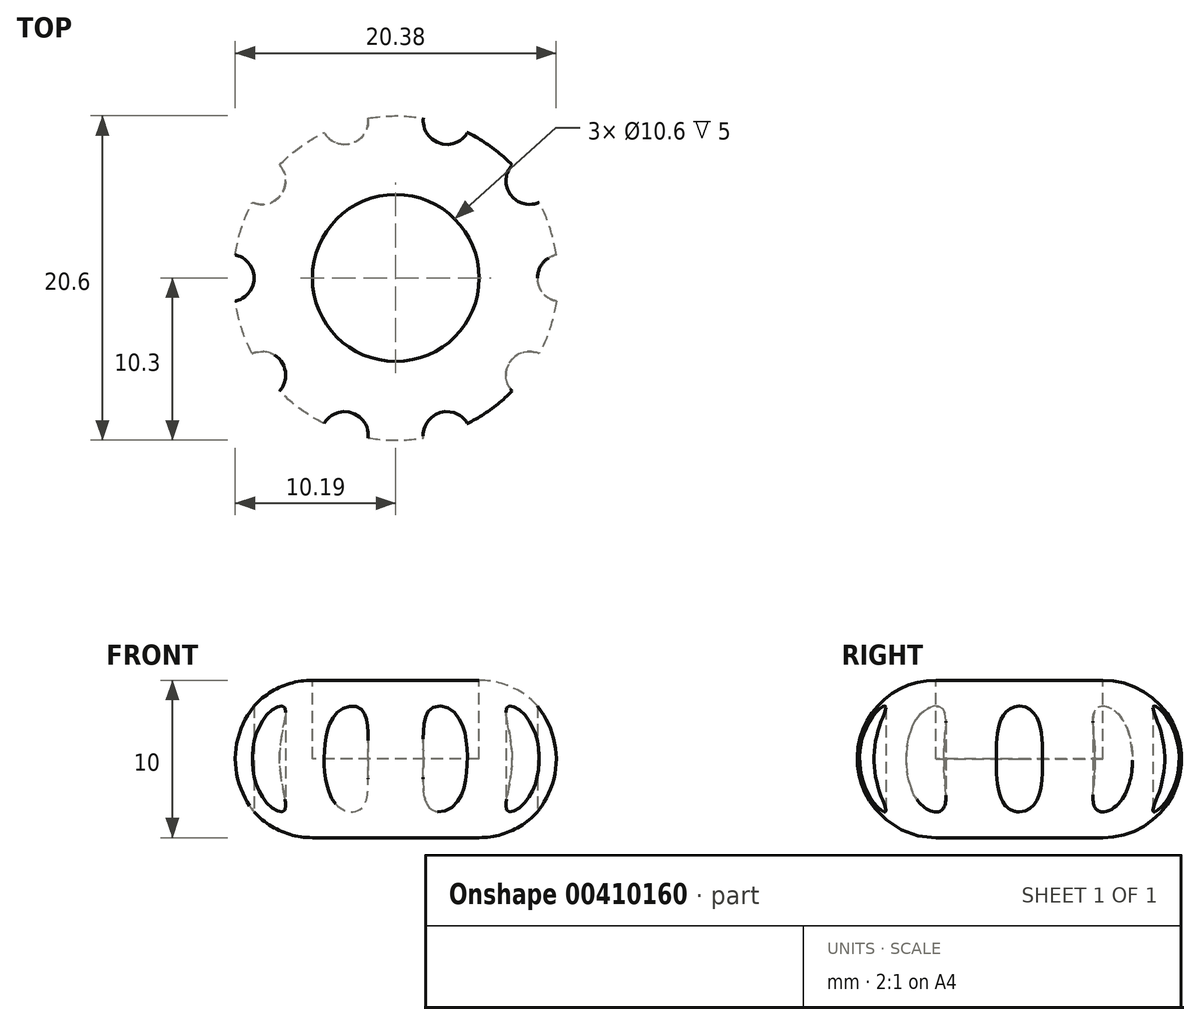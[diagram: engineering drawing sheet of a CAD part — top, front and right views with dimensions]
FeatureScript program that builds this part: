
annotation { "Feature Type Name" : "Feature", "Feature Type Description" : "" }
export const myFeature = defineFeature(function(context is Context, id is Id, definition is map)
    precondition{}
    {
        {
            var Q0;
            Q0=qCreatedBy(makeId("Front.planeOp"),FACE);
            var sketch = newSketch(context, id + "F0", { "sketchPlane" : qUnion([Q0])});
            skLineSegment(sketch, "E0", {"start": v(0, 0) * mm, "end": v(-5.3, 0) * mm});
            skLineSegment(sketch, "E1", {"start": v(-10.3, 5) * mm, "end": v(-10.3, 5) * mm});
            skLineSegment(sketch, "E2", {"start": v(-5.3, 10) * mm, "end": v(-5.3, 10) * mm});
            skLineSegment(sketch, "E3", {"start": v(-5.3, 10) * mm, "end": v(-5.3, 5) * mm});
            skLineSegment(sketch, "E4", {"start": v(-5.3, 5) * mm, "end": v(0, 5) * mm});
            skLineSegment(sketch, "E5", {"start": v(0, 5) * mm, "end": v(0, 0) * mm});
            skPoint(sketch, "E6.visualSharp", {"position": v(-10.3, 10) * mm});
            skArc(sketch, "E6.filletArc", {"start": v(-5.3, 10) * mm, "mid": v(-8.84, 8.54) * mm, "end": v(-10.3, 5) * mm});
            skPoint(sketch, "E7.visualSharp", {"position": v(-10.3, 0) * mm});
            skArc(sketch, "E7.filletArc", {"start": v(-10.3, 5) * mm, "mid": v(-8.84, 1.46) * mm, "end": v(-5.3, 0) * mm});
            skSolve(sketch);
        }
        {
            var Q0;
            Q0=makeQuery(id+"F0.imprint","IMPRINT",FACE,{"disambiguationData":[TD([[makeQuery(id+"F0.imprint","IMPRINT",EDGE,{"derivedFrom":sQuery(id+"F0.wireOp",EDGE,"E0")}),-1.0]])]});
            var Q1;
            Q1=sQuery(id+"F0.wireOp",EDGE,"E5");
            revolve(context, id + "F1", {"entities" : qUnion([Q0]), "axis" : qUnion([Q1]), "revolveType" : RevolveType.FULL});
        }
        {
            var Q0;
            Q0=makeQuery(id+"F1.opRevolve","SWEPT_FACE",FACE,{"disambiguationData":[OSD([sQuery(id+"F0.wireOp",EDGE,"E0")])]});
            var sketch = newSketch(context, id + "F2", { "sketchPlane" : qUnion([Q0])});
            skLineSegment(sketch, "E8", {"start": v(0, 0) * mm, "end": v(-16.48, 0) * mm, "construction": true});
            skCircle(sketch, "E9", {"center": v(-10.5, 0) * mm, "radius": 1.5 * mm});
            skCircle(sketch, "E10.1.0", {"center": v(-8.5, -6.17) * mm, "radius": 1.5 * mm});
            skCircle(sketch, "E10.2.0", {"center": v(-3.24, -9.99) * mm, "radius": 1.5 * mm});
            skCircle(sketch, "E10.3.0", {"center": v(3.24, -9.99) * mm, "radius": 1.5 * mm});
            skCircle(sketch, "E10.4.0", {"center": v(8.5, -6.17) * mm, "radius": 1.5 * mm});
            skCircle(sketch, "E10.5.0", {"center": v(10.5, 0) * mm, "radius": 1.5 * mm});
            skCircle(sketch, "E10.6.0", {"center": v(8.5, 6.17) * mm, "radius": 1.5 * mm});
            skCircle(sketch, "E10.7.0", {"center": v(3.24, 9.99) * mm, "radius": 1.5 * mm});
            skCircle(sketch, "E10.8.0", {"center": v(-3.24, 9.99) * mm, "radius": 1.5 * mm});
            skCircle(sketch, "E10.9.0", {"center": v(-8.5, 6.17) * mm, "radius": 1.5 * mm});
            skPoint(sketch, "E10.center", {"position": v(0, 0) * mm});
            skSolve(sketch);
        }
        {
            var Q0;
            Q0=makeQuery(id+"F2.imprint","IMPRINT",FACE,{"disambiguationData":[TD([[makeQuery(id+"F2.imprint","IMPRINT",EDGE,{"derivedFrom":sQuery(id+"F2.wireOp",EDGE,"E10.6.0")}),1.0]])]});
            var Q1;
            Q1=makeQuery(id+"F2.imprint","IMPRINT",FACE,{"disambiguationData":[TD([[makeQuery(id+"F2.imprint","IMPRINT",EDGE,{"derivedFrom":sQuery(id+"F2.wireOp",EDGE,"E10.5.0")}),1.0]])]});
            var Q2;
            Q2=makeQuery(id+"F2.imprint","IMPRINT",FACE,{"disambiguationData":[TD([[makeQuery(id+"F2.imprint","IMPRINT",EDGE,{"derivedFrom":sQuery(id+"F2.wireOp",EDGE,"E10.4.0")}),1.0]])]});
            var Q3;
            Q3=makeQuery(id+"F2.imprint","IMPRINT",FACE,{"disambiguationData":[TD([[makeQuery(id+"F2.imprint","IMPRINT",EDGE,{"derivedFrom":sQuery(id+"F2.wireOp",EDGE,"E10.3.0")}),1.0]])]});
            var Q4;
            Q4=makeQuery(id+"F2.imprint","IMPRINT",FACE,{"disambiguationData":[TD([[makeQuery(id+"F2.imprint","IMPRINT",EDGE,{"derivedFrom":sQuery(id+"F2.wireOp",EDGE,"E10.2.0")}),1.0]])]});
            var Q5;
            Q5=makeQuery(id+"F2.imprint","IMPRINT",FACE,{"disambiguationData":[TD([[makeQuery(id+"F2.imprint","IMPRINT",EDGE,{"derivedFrom":sQuery(id+"F2.wireOp",EDGE,"E10.1.0")}),1.0]])]});
            var Q6;
            Q6=makeQuery(id+"F2.imprint","IMPRINT",FACE,{"disambiguationData":[TD([[makeQuery(id+"F2.imprint","IMPRINT",EDGE,{"derivedFrom":sQuery(id+"F2.wireOp",EDGE,"E9")}),1.0]])]});
            var Q7;
            Q7=makeQuery(id+"F2.imprint","IMPRINT",FACE,{"disambiguationData":[TD([[makeQuery(id+"F2.imprint","IMPRINT",EDGE,{"derivedFrom":sQuery(id+"F2.wireOp",EDGE,"E10.9.0")}),1.0]])]});
            var Q8;
            Q8=makeQuery(id+"F2.imprint","IMPRINT",FACE,{"disambiguationData":[TD([[makeQuery(id+"F2.imprint","IMPRINT",EDGE,{"derivedFrom":sQuery(id+"F2.wireOp",EDGE,"E10.8.0")}),1.0]])]});
            var Q9;
            Q9=makeQuery(id+"F2.imprint","IMPRINT",FACE,{"disambiguationData":[TD([[makeQuery(id+"F2.imprint","IMPRINT",EDGE,{"derivedFrom":sQuery(id+"F2.wireOp",EDGE,"E10.7.0")}),1.0]])]});
            extrude(context, id + "F3", {"entities" : qUnion([Q0, Q1, Q2, Q3, Q4, Q5, Q6, Q7, Q8, Q9]), "operationType" : NewBodyOperationType.REMOVE, "oppositeDirection" : true, "depth" : 10 * mm});
        }
    });
